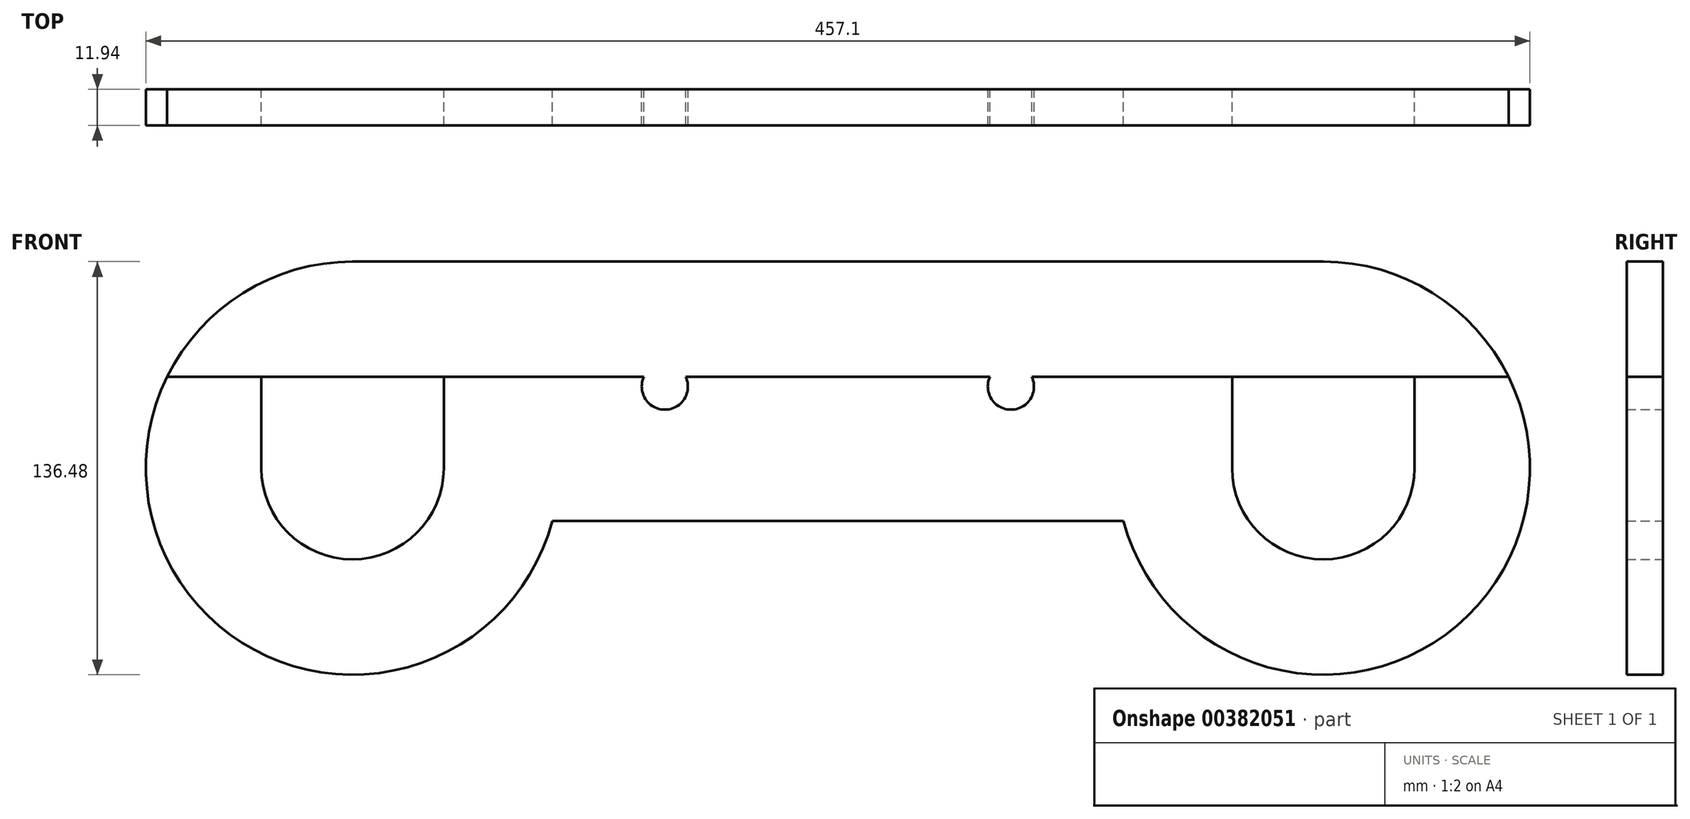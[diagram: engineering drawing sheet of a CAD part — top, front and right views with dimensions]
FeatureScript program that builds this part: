
annotation { "Feature Type Name" : "Feature", "Feature Type Description" : "" }
export const myFeature = defineFeature(function(context is Context, id is Id, definition is map)
    precondition{}
    {
        {
            var Q0;
            Q0=qCreatedBy(makeId("Front.planeOp"),FACE);
            var sketch = newSketch(context, id + "F0", { "sketchPlane" : qUnion([Q0])});
            skArc(sketch, "E0", {"start": v(-30.14, 0) * mm, "mid": v(0, -30.14) * mm, "end": v(30.14, 0) * mm});
            skLineSegment(sketch, "E1", {"start": v(0, 0) * mm, "end": v(30.14, 0) * mm, "construction": true});
            skLineSegment(sketch, "E2", {"start": v(30.14, 0) * mm, "end": v(290.49, 0) * mm, "construction": true});
            skLineSegment(sketch, "E3", {"start": v(290.49, 0) * mm, "end": v(320.62, 0) * mm, "construction": true});
            skArc(sketch, "E4", {"start": v(290.49, 0) * mm, "mid": v(320.62, -30.14) * mm, "end": v(350.76, 0) * mm});
            skLineSegment(sketch, "E5", {"start": v(160.31, 0) * mm, "end": v(160.31, 57.54) * mm, "construction": true});
            skLineSegment(sketch, "E6", {"start": v(160.31, -17.44) * mm, "end": v(65.97, -17.44) * mm});
            skLineSegment(sketch, "E7", {"start": v(160.31, -17.44) * mm, "end": v(254.65, -17.44) * mm});
            skArc(sketch, "E8", {"start": v(0, 68.24) * mm, "mid": v(-54.07, -41.63) * mm, "end": v(65.97, -17.44) * mm});
            skArc(sketch, "E9.MirrorCS", {"start": v(320.62, 68.24) * mm, "mid": v(374.69, -41.63) * mm, "end": v(254.65, -17.44) * mm});
            skLineSegment(sketch, "E10", {"start": v(0, 68.24) * mm, "end": v(320.62, 68.24) * mm});
            skPoint(sketch, "E11.trimOffspring.end.orphan", {"position": v(0, -68.24) * mm});
            skPoint(sketch, "E12.MirrorP", {"position": v(320.62, -68.24) * mm});
            skPoint(sketch, "E13.trimOffspring.end.orphan", {"position": v(0, 30.14) * mm});
            skPoint(sketch, "E14.end.orphan", {"position": v(0, 42) * mm});
            skPoint(sketch, "E15.end.orphan", {"position": v(0, 56.37) * mm});
            skPoint(sketch, "E16.MirrorCS.end.orphan", {"position": v(320.62, 30.14) * mm});
            skPoint(sketch, "E16.MirrorCS.start.orphan", {"position": v(320.62, 42) * mm});
            skPoint(sketch, "E17.MirrorCS.start.orphan", {"position": v(320.62, 56.37) * mm});
            skPoint(sketch, "E18.MirrorCS.start.orphan", {"position": v(320.62, 68.24) * mm});
            skLineSegment(sketch, "E19", {"start": v(0, 30.14) * mm, "end": v(96.24, 30.14) * mm});
            skLineSegment(sketch, "E20", {"start": v(0, 30.14) * mm, "end": v(-61.22, 30.14) * mm});
            skPoint(sketch, "E21.end.orphan", {"position": v(0, -56.37) * mm});
            skPoint(sketch, "E22.trimOffspring.end.orphan", {"position": v(0, -42) * mm});
            skPoint(sketch, "E22.trimOffspring.start.orphan", {"position": v(0, -30.14) * mm});
            skPoint(sketch, "E23.MirrorCS.end.orphan", {"position": v(320.62, -56.37) * mm});
            skPoint(sketch, "E23.MirrorCS.start.orphan", {"position": v(320.62, -42) * mm});
            skPoint(sketch, "E24.MirrorCS.start.orphan", {"position": v(320.62, -30.14) * mm});
            skArc(sketch, "E25", {"start": v(96.24, 30.14) * mm, "mid": v(103.16, 19.34) * mm, "end": v(110.09, 30.14) * mm});
            skLineSegment(sketch, "E26.trimOffspring", {"start": v(110.09, 30.14) * mm, "end": v(210.54, 30.14) * mm});
            skArc(sketch, "E27.MirrorCS", {"start": v(224.39, 30.14) * mm, "mid": v(217.46, 19.34) * mm, "end": v(210.54, 30.14) * mm});
            skLineSegment(sketch, "E28.trimOffspring", {"start": v(224.39, 30.14) * mm, "end": v(381.85, 30.14) * mm});
            skLineSegment(sketch, "E29", {"start": v(-30.14, 0) * mm, "end": v(-30.14, 30.14) * mm});
            skLineSegment(sketch, "E30", {"start": v(30.14, 0) * mm, "end": v(30.14, 30.14) * mm});
            skLineSegment(sketch, "E31.MirrorCS", {"start": v(290.49, 0) * mm, "end": v(290.49, 30.14) * mm});
            skLineSegment(sketch, "E32.MirrorCS", {"start": v(350.76, 0) * mm, "end": v(350.76, 30.14) * mm});
            skSolve(sketch);
        }
        {
            var Q0;
            {var subQ0=sQuery(id+"F0.wireOp",EDGE,"E10");Q0=makeQuery(id+"F0.imprint","IMPRINT",FACE,{"disambiguationData":[TD([[makeQuery(id+"F0.imprint","IMPRINT",EDGE,{"derivedFrom":subQ0}),-1.0]])]});}
            extrude(context, id + "F1", {"entities" : qUnion([Q0]), "depth" : 11.94 * mm});
        }
        {
            var Q0;
            Q0=makeQuery(id+"F0.imprint","IMPRINT",FACE,{"disambiguationData":[TD([[makeQuery(id+"F0.imprint","IMPRINT",EDGE,{"derivedFrom":sQuery(id+"F0.wireOp",EDGE,"E0")}),-1.0]])]});
            extrude(context, id + "F2", {"entities" : qUnion([Q0]), "depth" : 11.94 * mm});
        }
    });
